# Revit family: Drinking_Fountain-Murdock-A131.8-VR_Series
name_source: partatom
category: Plumbing Fixtures
units: mm (PartAtom-declared; Revit-internal decimal feet)

## family parameters
Cut with Voids When Loaded = Yes
Host = Face
OmniClass Number = 23.65.70.14.11
OmniClass Title = Drinking Fountains/Coolers
Part Type = Normal
Room Calculation Point = No
Round Connector Dimension = Use Diameter
Shared = Yes

## types (6) — shared parameters
220V - 220 volt / 50 Hz compressor = No
ADA Compliant = Yes
Assembly Code = D2010810
CW Connection = Yes
CWFU = 1.5
Default Elevation = 0"
Description = Vandal-Resistant, Wall-Mounted, Oval Drinking Fountain - In-Wall Refrigeration (8GPH), ADA, Stainless Steel
Flow Rate = 8.0  GPH
Full Load Amps = 4.6
HP - High polished stainless steel = No
HW Connection = No
Height = 39 1/4"
IAPMO Compliance = ANSI/ASHRAE 18, cUPC, IAPMO tested to NSF/ANSI 61, Section 9, UL Listed (US and Canada)
Inlet Connection Diameter = 3/8"
Installation Type = Recessed Wall Mounted
Length = 21"
Manufacturer = Murdock Manufacturing
Outlet Connection Diameter = 1 1/4"
Product Documentation Link = https://www.murdockmfg.com
Product Page URL = https://www.murdockmfg.com
Rated Watts = 390
Shipping Weight = 90 Lbs.
URL = https://www.murdockmfg.com
Vent Connection = No
WF1 - 1500 gallon capacity, NSF 42+53, 1 micron lead reduction filter = No
WFU = 2
Waste Connection = Yes
Water Pressure = pressure range of 20-105 psig
Width = 29 1/4"
cUPC Compliant = Yes
zero-valued in all types: HWFU

## per-type parameters (varying)
| type | Bubbler Material | F - Flexible bubbler | Finish | Material | S - Lead-Free Stainless Steel |
| A131308F-VR | Murdock- White | Yes | Stainless Steel-Murdock-High Polish Gold | Stainless Steel-Murdock-High Polish Gold | No |
| A131208F-VR | Murdock- White | Yes | Stainless Steel-Murdock-Bronze | Stainless Steel-Murdock-Bronze | No |
| A131408F-VR | Murdock- White | Yes | Stainless Steel-Murdock-Brushed Satin | Stainless Steel-Murdock-Brushed Satin | No |
| A131208S-VR | Stainless Steel-Murdock-Bronze | No | Stainless Steel-Murdock-Bronze | Stainless Steel-Murdock-Bronze | Yes |
| A131308S-VR | Stainless Steel-Murdock-High Polish Gold | No | Stainless Steel-Murdock-High Polish Gold | Stainless Steel-Murdock-High Polish Gold | Yes |
| A131408S-VR | Stainless Steel-Murdock-Brushed Satin | No | Stainless Steel-Murdock-Brushed Satin | Stainless Steel-Murdock-Brushed Satin | Yes |

note: column(s) folded — value = type name in every type: Model

## geometry (parser evidence)
native form markers: Sweep x6
no freeform markers — native parametric forms only
